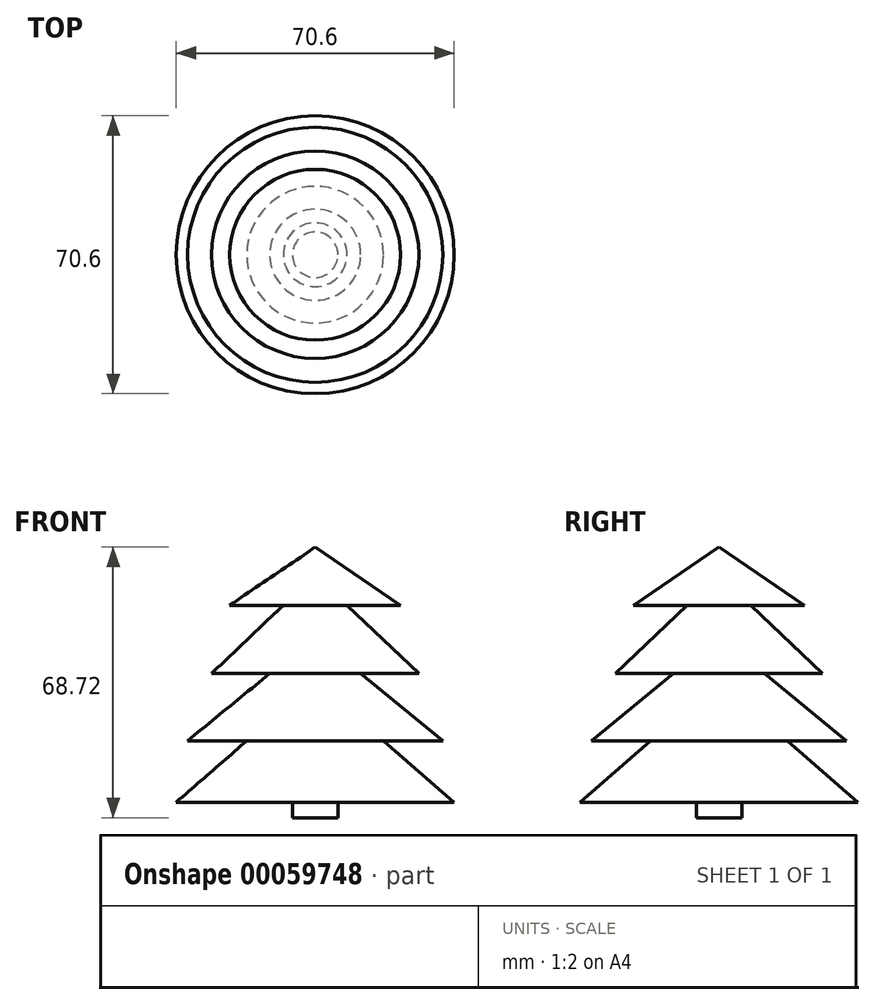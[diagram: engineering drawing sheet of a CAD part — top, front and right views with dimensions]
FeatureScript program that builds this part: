
annotation { "Feature Type Name" : "Feature", "Feature Type Description" : "" }
export const myFeature = defineFeature(function(context is Context, id is Id, definition is map)
    precondition{}
    {
        {
            var Q0;
            Q0=qCreatedBy(makeId("Front.planeOp"),FACE);
            var sketch = newSketch(context, id + "F0", { "sketchPlane" : qUnion([Q0])});
            skLineSegment(sketch, "E0", {"start": v(0, 0) * mm, "end": v(0, 68.72) * mm});
            skLineSegment(sketch, "E1", {"start": v(0, 68.72) * mm, "end": v(21.7, 53.97) * mm});
            skLineSegment(sketch, "E2", {"start": v(21.7, 53.97) * mm, "end": v(8.1, 53.97) * mm});
            skLineSegment(sketch, "E3", {"start": v(8.1, 53.97) * mm, "end": v(26.33, 36.6) * mm});
            skLineSegment(sketch, "E4", {"start": v(26.33, 36.6) * mm, "end": v(11.57, 36.6) * mm});
            skLineSegment(sketch, "E5", {"start": v(11.57, 36.6) * mm, "end": v(32.4, 19.53) * mm});
            skLineSegment(sketch, "E6", {"start": v(32.4, 19.53) * mm, "end": v(17.36, 19.53) * mm});
            skLineSegment(sketch, "E7", {"start": v(17.36, 19.53) * mm, "end": v(35.3, 3.9) * mm});
            skLineSegment(sketch, "E8", {"start": v(35.3, 3.9) * mm, "end": v(5.79, 3.9) * mm});
            skLineSegment(sketch, "E9", {"start": v(5.79, 3.9) * mm, "end": v(5.79, 0) * mm});
            skLineSegment(sketch, "E10", {"start": v(5.79, 0) * mm, "end": v(0, 0) * mm});
            skSolve(sketch);
        }
        {
            var Q0;
            Q0 = qSketchRegion(id + "F0", true);
            var Q1;
            Q1=sQuery(id+"F0.wireOp",EDGE,"E0");
            revolve(context, id + "F1", {"entities" : qUnion([Q0]), "axis" : qUnion([Q1]), "revolveType" : RevolveType.FULL});
        }
    });
